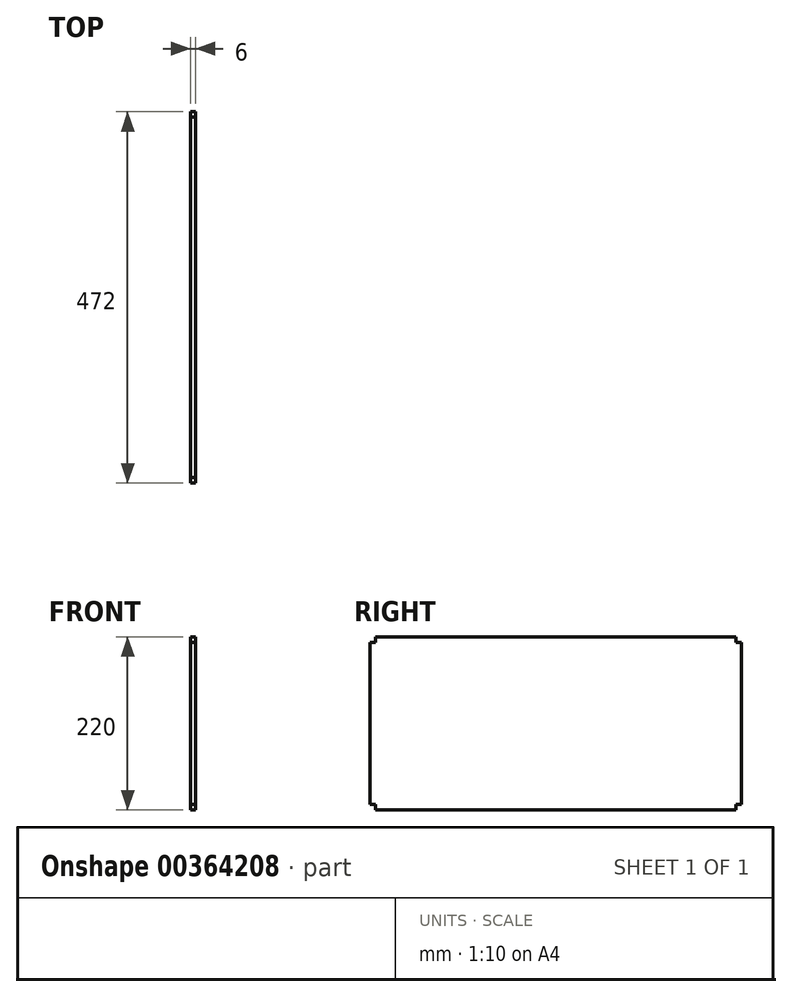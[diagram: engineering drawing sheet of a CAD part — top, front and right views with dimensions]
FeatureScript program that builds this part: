
annotation { "Feature Type Name" : "Feature", "Feature Type Description" : "" }
export const myFeature = defineFeature(function(context is Context, id is Id, definition is map)
    precondition{}
    {
        {
            var Q0;
            Q0=qCreatedBy(makeId("Right.planeOp"),FACE);
            var sketch = newSketch(context, id + "F0", { "sketchPlane" : qUnion([Q0])});
            skLineSegment(sketch, "E0.bottom", {"start": v(229, -110) * mm, "end": v(-229, -110) * mm});
            skLineSegment(sketch, "E0.top", {"start": v(229, 110) * mm, "end": v(-229, 110) * mm});
            skLineSegment(sketch, "E0.left", {"start": v(236, -103) * mm, "end": v(236, 103) * mm});
            skLineSegment(sketch, "E0.right", {"start": v(-236, -103) * mm, "end": v(-236, 103) * mm});
            skPoint(sketch, "E0.middle", {"position": v(0, 0) * mm});
            skPoint(sketch, "E1.orphan", {"position": v(-236, 110) * mm});
            skLineSegment(sketch, "E2.bottom", {"start": v(229, -103) * mm, "end": v(236, -103) * mm});
            skLineSegment(sketch, "E2.left", {"start": v(229, -103) * mm, "end": v(229, -110) * mm});
            skPoint(sketch, "E2.middle", {"position": v(236, -110) * mm});
            skLineSegment(sketch, "E3.bottom", {"start": v(236, 103) * mm, "end": v(229, 103) * mm});
            skLineSegment(sketch, "E3.right", {"start": v(229, 103) * mm, "end": v(229, 110) * mm});
            skPoint(sketch, "E3.middle", {"position": v(236, 110) * mm});
            skLineSegment(sketch, "E4.top", {"start": v(-229, -103) * mm, "end": v(-236, -103) * mm});
            skLineSegment(sketch, "E4.left", {"start": v(-229, -110) * mm, "end": v(-229, -103) * mm});
            skPoint(sketch, "E4.middle", {"position": v(-236, -110) * mm});
            skPoint(sketch, "E3.left.start.orphan", {"position": v(243, 103) * mm});
            skPoint(sketch, "E3.top.end.orphan", {"position": v(229, 117) * mm});
            skPoint(sketch, "E3.top.start.orphan", {"position": v(243, 117) * mm});
            skPoint(sketch, "E2.top.start.orphan", {"position": v(229, -117) * mm});
            skPoint(sketch, "E2.right.end.orphan", {"position": v(243, -117) * mm});
            skPoint(sketch, "E2.right.start.orphan", {"position": v(243, -103) * mm});
            skPoint(sketch, "E4.bottom.start.orphan", {"position": v(-229, -117) * mm});
            skPoint(sketch, "E4.right.end.orphan", {"position": v(-243, -103) * mm});
            skPoint(sketch, "E4.right.start.orphan", {"position": v(-243, -117) * mm});
            skLineSegment(sketch, "E5.bottom", {"start": v(-229, 103) * mm, "end": v(-236, 103) * mm});
            skLineSegment(sketch, "E5.left", {"start": v(-229, 103) * mm, "end": v(-229, 110) * mm});
            skPoint(sketch, "E5.top.start.orphan", {"position": v(-229, 117) * mm});
            skPoint(sketch, "E5.right.end.orphan", {"position": v(-243, 117) * mm});
            skPoint(sketch, "E6.orphan", {"position": v(-243, 103) * mm});
            skSolve(sketch);
        }
        {
            var Q0;
            Q0=makeQuery(id+"F0.imprint","IMPRINT",FACE,{"disambiguationData":[TD([[makeQuery(id+"F0.imprint","IMPRINT",EDGE,{"derivedFrom":sQuery(id+"F0.wireOp",EDGE,"E0.bottom")}),-1.0]])]});
            extrude(context, id + "F1", {"entities" : qUnion([Q0]), "depth" : 6 * mm});
        }
    });
